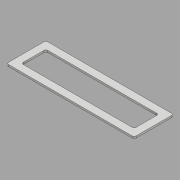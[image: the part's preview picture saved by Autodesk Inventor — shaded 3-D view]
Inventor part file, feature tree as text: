
AUTODESK INVENTOR PART (.ipt)
format: ipt  version: 2017 (Build 210142000, 142)  size: 97,280 bytes
history: native  units: mm
features: extrude x2, sketch x2, other x1, fillet x1
ambient origin geometry x8: Origin, YZ Plane, XZ Plane, XY Plane, X Axis, Y Axis, Z Axis, Center Point
bodies: Body1 (feature_tree)
feature tree (6):
  other  "ソリッド1"
  extrude  "押し出し1"  Depth=130.0mm
  extrude  "押し出し2"  Depth=40.0mm
  fillet  "フィレット1"  Radius=2.0mm
  sketch  "スケッチ1"
  sketch  "スケッチ2"
